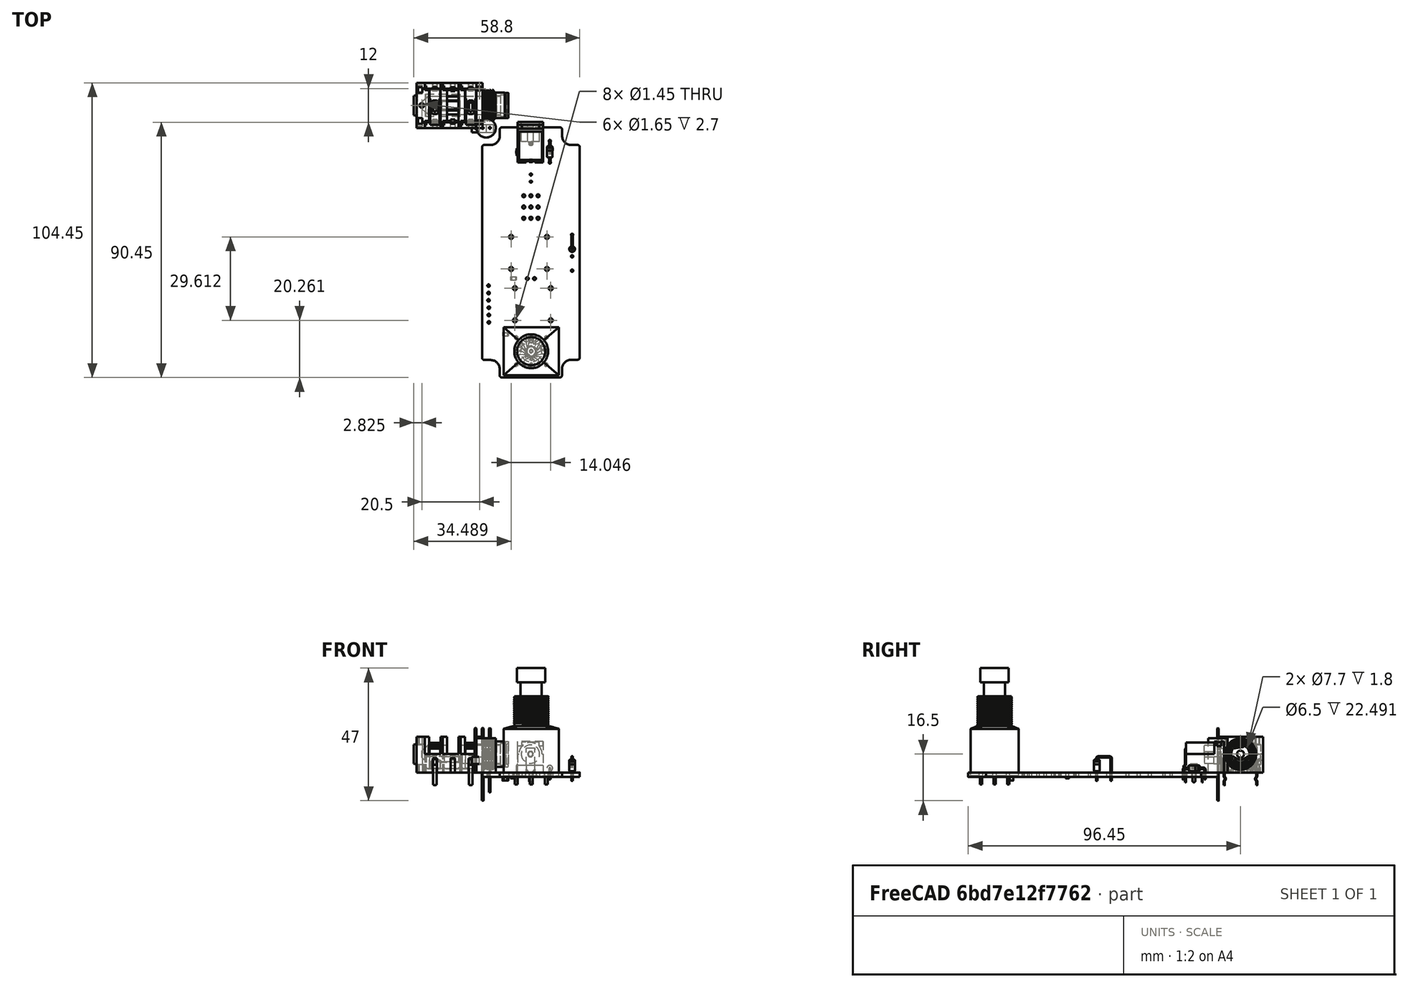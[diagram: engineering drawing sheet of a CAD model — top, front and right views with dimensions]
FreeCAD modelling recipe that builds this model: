
FCSTD DOCUMENT  (FreeCAD 0.20R25645 (Git))
Label: freecad_pcb
License: All rights reserved
LicenseURL: http://en.wikipedia.org/wiki/All_rights_reserved
objects: App::Link×31, Part::Feature×22, App::Part×8, PartDesign::CoordinateSystem×1, Sketcher::SketchObject×1
note: 24 computed .brp shape members not serialized (recipe doc carries the construction recipe); baked Part::Feature solids carry a one-line shape summary decoded from their .brp

FEATURE [PartDesign::CoordinateSystem] Local_CS_ba79
  AttacherType = Attacher::AttachEngine3D
FEATURE [Part::Feature] Pcb_ba79
  Placement = pos=(-82.9,55.9,0) rot=(0,0,1;0rad)
  shape: bbox 34.6 x 88.7 x 1.6 mm, 142 faces (baked)
FEATURE [Sketcher::SketchObject] PCB_Sketch_ba79
  FullyConstrained = false
  sketch-geometry (464):
    g0: LineSegment StartX=33.6003 StartY=-6 StartZ=0 EndX=31.35 EndY=-6 EndZ=0
    g1: LineSegment StartX=34.4 StartY=-81.3503 StartZ=0 EndX=34.4 EndY=-6.79966 EndZ=0
    g2: LineSegment StartX=31.35 StartY=-82.15 StartZ=0 EndX=33.6003 EndY=-82.15 EndZ=0
    g3: LineSegment StartX=28.1 StartY=-87.6503 StartZ=0 EndX=28.1 EndY=-85.4 EndZ=0
    g4: LineSegment StartX=6.79966 StartY=-88.45 StartZ=0 EndX=27.3003 EndY=-88.45 EndZ=0
    g5: LineSegment StartX=-0.2 StartY=-6.79966 StartZ=0 EndX=-0.2 EndY=-81.4503 EndZ=0
    g6: LineSegment StartX=0.599657 StartY=-82.25 StartZ=0 EndX=2.85 EndY=-82.25 EndZ=0
    g7: LineSegment StartX=6 StartY=-85.4 StartZ=0 EndX=6 EndY=-87.6503 EndZ=0
    g8: LineSegment StartX=28.15 StartY=-2.8 StartZ=0 EndX=28.15 EndY=-0.549657 EndZ=0
    g9: LineSegment StartX=27.3503 StartY=0.25 StartZ=0 EndX=6.84966 EndY=0.25 EndZ=0
    g10: LineSegment StartX=6.05 StartY=-0.549657 StartZ=0 EndX=6.05 EndY=-2.8 EndZ=0
    g11: LineSegment StartX=2.85 StartY=-6 StartZ=0 EndX=0.599657 EndY=-6 EndZ=0
    g12: BSplineCurve PolesCount=4 KnotsCount=2 Degree=3 IsPeriodic=0
    g13: BSplineCurve PolesCount=4 KnotsCount=2 Degree=3 IsPeriodic=0
    g14: BSplineCurve PolesCount=4 KnotsCount=2 Degree=3 IsPeriodic=0
    g15: BSplineCurve PolesCount=4 KnotsCount=2 Degree=3 IsPeriodic=0
    g16: BSplineCurve PolesCount=4 KnotsCount=2 Degree=3 IsPeriodic=0
    g17: BSplineCurve PolesCount=4 KnotsCount=2 Degree=3 IsPeriodic=0
    g18: BSplineCurve PolesCount=4 KnotsCount=2 Degree=3 IsPeriodic=0
    g19: BSplineCurve PolesCount=4 KnotsCount=2 Degree=3 IsPeriodic=0
    g20: BSplineCurve PolesCount=4 KnotsCount=2 Degree=3 IsPeriodic=0
    g21: BSplineCurve PolesCount=4 KnotsCount=2 Degree=3 IsPeriodic=0
    g22: BSplineCurve PolesCount=4 KnotsCount=2 Degree=3 IsPeriodic=0
    g23: BSplineCurve PolesCount=4 KnotsCount=2 Degree=3 IsPeriodic=0
    g24: BSplineCurve PolesCount=4 KnotsCount=2 Degree=3 IsPeriodic=0
    g25: BSplineCurve PolesCount=4 KnotsCount=2 Degree=3 IsPeriodic=0
    g26: BSplineCurve PolesCount=4 KnotsCount=2 Degree=3 IsPeriodic=0
    g27: BSplineCurve PolesCount=4 KnotsCount=2 Degree=3 IsPeriodic=0
    g28: BSplineCurve PolesCount=4 KnotsCount=2 Degree=3 IsPeriodic=0
    g29: BSplineCurve PolesCount=4 KnotsCount=2 Degree=3 IsPeriodic=0
    g30: BSplineCurve PolesCount=4 KnotsCount=2 Degree=3 IsPeriodic=0
    g31: BSplineCurve PolesCount=4 KnotsCount=2 Degree=3 IsPeriodic=0
    g32: BSplineCurve PolesCount=4 KnotsCount=2 Degree=3 IsPeriodic=0
    g33: BSplineCurve PolesCount=4 KnotsCount=2 Degree=3 IsPeriodic=0
    g34: BSplineCurve PolesCount=4 KnotsCount=2 Degree=3 IsPeriodic=0
    g35: BSplineCurve PolesCount=4 KnotsCount=2 Degree=3 IsPeriodic=0
    g36: BSplineCurve PolesCount=4 KnotsCount=2 Degree=3 IsPeriodic=0
    g37: BSplineCurve PolesCount=4 KnotsCount=2 Degree=3 IsPeriodic=0
    g38: BSplineCurve PolesCount=4 KnotsCount=2 Degree=3 IsPeriodic=0
    g39: BSplineCurve PolesCount=4 KnotsCount=2 Degree=3 IsPeriodic=0
    g40: BSplineCurve PolesCount=4 KnotsCount=2 Degree=3 IsPeriodic=0
    g41: BSplineCurve PolesCount=4 KnotsCount=2 Degree=3 IsPeriodic=0
    g42: BSplineCurve PolesCount=4 KnotsCount=2 Degree=3 IsPeriodic=0
    g43: BSplineCurve PolesCount=4 KnotsCount=2 Degree=3 IsPeriodic=0
    g44: BSplineCurve PolesCount=4 KnotsCount=2 Degree=3 IsPeriodic=0
    g45: BSplineCurve PolesCount=4 KnotsCount=2 Degree=3 IsPeriodic=0
    g46: BSplineCurve PolesCount=4 KnotsCount=2 Degree=3 IsPeriodic=0
    g47: BSplineCurve PolesCount=4 KnotsCount=2 Degree=3 IsPeriodic=0
    g48: BSplineCurve PolesCount=4 KnotsCount=2 Degree=3 IsPeriodic=0
    g49: BSplineCurve PolesCount=4 KnotsCount=2 Degree=3 IsPeriodic=0
    g50: BSplineCurve PolesCount=4 KnotsCount=2 Degree=3 IsPeriodic=0
    g51: BSplineCurve PolesCount=4 KnotsCount=2 Degree=3 IsPeriodic=0
    g52: BSplineCurve PolesCount=4 KnotsCount=2 Degree=3 IsPeriodic=0
    g53: BSplineCurve PolesCount=4 KnotsCount=2 Degree=3 IsPeriodic=0
    g54: BSplineCurve PolesCount=4 KnotsCount=2 Degree=3 IsPeriodic=0
    g55: BSplineCurve PolesCount=4 KnotsCount=2 Degree=3 IsPeriodic=0
    g56: BSplineCurve PolesCount=4 KnotsCount=2 Degree=3 IsPeriodic=0
    g57: BSplineCurve PolesCount=4 KnotsCount=2 Degree=3 IsPeriodic=0
    g58: BSplineCurve PolesCount=4 KnotsCount=2 Degree=3 IsPeriodic=0
    g59: BSplineCurve PolesCount=4 KnotsCount=2 Degree=3 IsPeriodic=0
    g60: BSplineCurve PolesCount=4 KnotsCount=2 Degree=3 IsPeriodic=0
    g61: BSplineCurve PolesCount=4 KnotsCount=2 Degree=3 IsPeriodic=0
    g62: BSplineCurve PolesCount=4 KnotsCount=2 Degree=3 IsPeriodic=0
    g63: BSplineCurve PolesCount=4 KnotsCount=2 Degree=3 IsPeriodic=0
    g64: BSplineCurve PolesCount=4 KnotsCount=2 Degree=3 IsPeriodic=0
    g65: BSplineCurve PolesCount=4 KnotsCount=2 Degree=3 IsPeriodic=0
    g66: BSplineCurve PolesCount=4 KnotsCount=2 Degree=3 IsPeriodic=0
    g67: BSplineCurve PolesCount=4 KnotsCount=2 Degree=3 IsPeriodic=0
    g68: BSplineCurve PolesCount=4 KnotsCount=2 Degree=3 IsPeriodic=0
    g69: BSplineCurve PolesCount=4 KnotsCount=2 Degree=3 IsPeriodic=0
    g70: BSplineCurve PolesCount=4 KnotsCount=2 Degree=3 IsPeriodic=0
    g71: BSplineCurve PolesCount=4 KnotsCount=2 Degree=3 IsPeriodic=0
    g72: BSplineCurve PolesCount=4 KnotsCount=2 Degree=3 IsPeriodic=0
    g73: BSplineCurve PolesCount=4 KnotsCount=2 Degree=3 IsPeriodic=0
    g74: BSplineCurve PolesCount=4 KnotsCount=2 Degree=3 IsPeriodic=0
    g75: BSplineCurve PolesCount=4 KnotsCount=2 Degree=3 IsPeriodic=0
    g76: ArcOfCircle CenterX=31.35 CenterY=-2.8 CenterZ=0 NormalX=0 NormalY=0 NormalZ=1 AngleXU=0 Radius=3.2 StartAngle=3.14159 EndAngle=4.71239
    g77: ArcOfCircle CenterX=31.35 CenterY=-85.4 CenterZ=0 NormalX=0 NormalY=0 NormalZ=1 AngleXU=0 Radius=3.25 StartAngle=1.5708 EndAngle=3.14159
    g78: ArcOfCircle CenterX=2.85 CenterY=-85.4 CenterZ=0 NormalX=0 NormalY=0 NormalZ=1 AngleXU=0 Radius=3.15 StartAngle=0 EndAngle=1.5708
    g79: ArcOfCircle CenterX=2.85 CenterY=-2.8 CenterZ=0 NormalX=0 NormalY=0 NormalZ=1 AngleXU=0 Radius=3.2 StartAngle=4.71239 EndAngle=6.28319
    g80-g83: Circle x4 (B-spline internal-alignment scaffolding for g12; pole/knot coordinates omitted)
    g84: GeomPoint X=34.3847 Y=-6.64376 Z=0
    g85: GeomPoint X=34.4 Y=-6.79966 Z=0
    g86-g89: Circle x4 (B-spline internal-alignment scaffolding for g13; pole/knot coordinates omitted)
    g90: GeomPoint X=34.3392 Y=-6.49375 Z=0
    g91: GeomPoint X=34.3847 Y=-6.64376 Z=0
    g92-g95: Circle x4 (B-spline internal-alignment scaffolding for g14; pole/knot coordinates omitted)
    g96: GeomPoint X=34.2653 Y=-6.35536 Z=0
    g97: GeomPoint X=34.3392 Y=-6.49375 Z=0
    g98-g101: Circle x4 (B-spline internal-alignment scaffolding for g15; pole/knot coordinates omitted)
    g102: GeomPoint X=34.1658 Y=-6.23417 Z=0
    g103: GeomPoint X=34.2653 Y=-6.35536 Z=0
    g104-g107: Circle x4 (B-spline internal-alignment scaffolding for g16; pole/knot coordinates omitted)
    g108: GeomPoint X=34.0446 Y=-6.13472 Z=0
    g109: GeomPoint X=34.1658 Y=-6.23417 Z=0
    g110-g113: Circle x4 (B-spline internal-alignment scaffolding for g17; pole/knot coordinates omitted)
    g114: GeomPoint X=33.9063 Y=-6.06079 Z=0
    g115: GeomPoint X=34.0446 Y=-6.13472 Z=0
    g116-g119: Circle x4 (B-spline internal-alignment scaffolding for g18; pole/knot coordinates omitted)
    g120: GeomPoint X=33.7562 Y=-6.01533 Z=0
    g121: GeomPoint X=33.9063 Y=-6.06079 Z=0
    g122-g125: Circle x4 (B-spline internal-alignment scaffolding for g19; pole/knot coordinates omitted)
    g126: GeomPoint X=33.6003 Y=-6 Z=0
    g127: GeomPoint X=33.7562 Y=-6.01533 Z=0
    g128-g131: Circle x4 (B-spline internal-alignment scaffolding for g20; pole/knot coordinates omitted)
    g132: GeomPoint X=33.7562 Y=-82.1347 Z=0
    g133: GeomPoint X=33.6003 Y=-82.15 Z=0
    g134-g137: Circle x4 (B-spline internal-alignment scaffolding for g21; pole/knot coordinates omitted)
    g138: GeomPoint X=33.9063 Y=-82.0892 Z=0
    g139: GeomPoint X=33.7562 Y=-82.1347 Z=0
    g140-g143: Circle x4 (B-spline internal-alignment scaffolding for g22; pole/knot coordinates omitted)
    g144: GeomPoint X=34.0446 Y=-82.0153 Z=0
    g145: GeomPoint X=33.9063 Y=-82.0892 Z=0
    g146-g149: Circle x4 (B-spline internal-alignment scaffolding for g23; pole/knot coordinates omitted)
    g150: GeomPoint X=34.1658 Y=-81.9158 Z=0
    g151: GeomPoint X=34.0446 Y=-82.0153 Z=0
    g152-g155: Circle x4 (B-spline internal-alignment scaffolding for g24; pole/knot coordinates omitted)
    g156: GeomPoint X=34.2653 Y=-81.7946 Z=0
    g157: GeomPoint X=34.1658 Y=-81.9158 Z=0
    g158-g161: Circle x4 (B-spline internal-alignment scaffolding for g25; pole/knot coordinates omitted)
    g162: GeomPoint X=34.3392 Y=-81.6563 Z=0
    g163: GeomPoint X=34.2653 Y=-81.7946 Z=0
    g164-g167: Circle x4 (B-spline internal-alignment scaffolding for g26; pole/knot coordinates omitted)
    g168: GeomPoint X=34.3847 Y=-81.5062 Z=0
    g169: GeomPoint X=34.3392 Y=-81.6563 Z=0
    g170-g173: Circle x4 (B-spline internal-alignment scaffolding for g27; pole/knot coordinates omitted)
    g174: GeomPoint X=34.4 Y=-81.3503 Z=0
    g175: GeomPoint X=34.3847 Y=-81.5062 Z=0
    g176-g179: Circle x4 (B-spline internal-alignment scaffolding for g28; pole/knot coordinates omitted)
    g180: GeomPoint X=27.4562 Y=-88.4347 Z=0
    g181: GeomPoint X=27.3003 Y=-88.45 Z=0
    g182-g185: Circle x4 (B-spline internal-alignment scaffolding for g29; pole/knot coordinates omitted)
    g186: GeomPoint X=27.6063 Y=-88.3892 Z=0
    g187: GeomPoint X=27.4562 Y=-88.4347 Z=0
    g188-g191: Circle x4 (B-spline internal-alignment scaffolding for g30; pole/knot coordinates omitted)
    g192: GeomPoint X=27.7446 Y=-88.3153 Z=0
    g193: GeomPoint X=27.6063 Y=-88.3892 Z=0
    g194-g197: Circle x4 (B-spline internal-alignment scaffolding for g31; pole/knot coordinates omitted)
    g198: GeomPoint X=27.8658 Y=-88.2158 Z=0
    g199: GeomPoint X=27.7446 Y=-88.3153 Z=0
    g200-g203: Circle x4 (B-spline internal-alignment scaffolding for g32; pole/knot coordinates omitted)
    g204: GeomPoint X=27.9653 Y=-88.0946 Z=0
    g205: GeomPoint X=27.8658 Y=-88.2158 Z=0
    g206-g209: Circle x4 (B-spline internal-alignment scaffolding for g33; pole/knot coordinates omitted)
    g210: GeomPoint X=28.0392 Y=-87.9563 Z=0
    g211: GeomPoint X=27.9653 Y=-88.0946 Z=0
    g212-g215: Circle x4 (B-spline internal-alignment scaffolding for g34; pole/knot coordinates omitted)
    g216: GeomPoint X=28.0847 Y=-87.8062 Z=0
    g217: GeomPoint X=28.0392 Y=-87.9563 Z=0
    g218-g221: Circle x4 (B-spline internal-alignment scaffolding for g35; pole/knot coordinates omitted)
    g222: GeomPoint X=28.1 Y=-87.6503 Z=0
    g223: GeomPoint X=28.0847 Y=-87.8062 Z=0
    g224-g227: Circle x4 (B-spline internal-alignment scaffolding for g36; pole/knot coordinates omitted)
    g228: GeomPoint X=-0.184668 Y=-81.6062 Z=0
    g229: GeomPoint X=-0.2 Y=-81.4503 Z=0
    g230-g233: Circle x4 (B-spline internal-alignment scaffolding for g37; pole/knot coordinates omitted)
    g234: GeomPoint X=-0.139209 Y=-81.7563 Z=0
    g235: GeomPoint X=-0.184668 Y=-81.6062 Z=0
    g236-g239: Circle x4 (B-spline internal-alignment scaffolding for g38; pole/knot coordinates omitted)
    g240: GeomPoint X=-0.065278 Y=-81.8946 Z=0
    g241: GeomPoint X=-0.139209 Y=-81.7563 Z=0
    g242-g245: Circle x4 (B-spline internal-alignment scaffolding for g39; pole/knot coordinates omitted)
    g246: GeomPoint X=0.034172 Y=-82.0158 Z=0
    g247: GeomPoint X=-0.065278 Y=-81.8946 Z=0
    g248-g251: Circle x4 (B-spline internal-alignment scaffolding for g40; pole/knot coordinates omitted)
    g252: GeomPoint X=0.155365 Y=-82.1153 Z=0
    g253: GeomPoint X=0.034172 Y=-82.0158 Z=0
    g254-g257: Circle x4 (B-spline internal-alignment scaffolding for g41; pole/knot coordinates omitted)
    g258: GeomPoint X=0.293747 Y=-82.1892 Z=0
    g259: GeomPoint X=0.155365 Y=-82.1153 Z=0
    g260-g263: Circle x4 (B-spline internal-alignment scaffolding for g42; pole/knot coordinates omitted)
    g264: GeomPoint X=0.443764 Y=-82.2347 Z=0
    g265: GeomPoint X=0.293747 Y=-82.1892 Z=0
    g266-g269: Circle x4 (B-spline internal-alignment scaffolding for g43; pole/knot coordinates omitted)
    g270: GeomPoint X=0.599657 Y=-82.25 Z=0
    g271: GeomPoint X=0.443764 Y=-82.2347 Z=0
    g272-g275: Circle x4 (B-spline internal-alignment scaffolding for g44; pole/knot coordinates omitted)
    g276: GeomPoint X=6.01533 Y=-87.8062 Z=0
    g277: GeomPoint X=6 Y=-87.6503 Z=0
    g278-g281: Circle x4 (B-spline internal-alignment scaffolding for g45; pole/knot coordinates omitted)
    g282: GeomPoint X=6.06079 Y=-87.9563 Z=0
    g283: GeomPoint X=6.01533 Y=-87.8062 Z=0
    g284-g287: Circle x4 (B-spline internal-alignment scaffolding for g46; pole/knot coordinates omitted)
    g288: GeomPoint X=6.13472 Y=-88.0946 Z=0
    g289: GeomPoint X=6.06079 Y=-87.9563 Z=0
    g290-g293: Circle x4 (B-spline internal-alignment scaffolding for g47; pole/knot coordinates omitted)
    g294: GeomPoint X=6.23417 Y=-88.2158 Z=0
    g295: GeomPoint X=6.13472 Y=-88.0946 Z=0
    g296-g299: Circle x4 (B-spline internal-alignment scaffolding for g48; pole/knot coordinates omitted)
    g300: GeomPoint X=6.35536 Y=-88.3153 Z=0
    g301: GeomPoint X=6.23417 Y=-88.2158 Z=0
    g302-g305: Circle x4 (B-spline internal-alignment scaffolding for g49; pole/knot coordinates omitted)
    g306: GeomPoint X=6.49375 Y=-88.3892 Z=0
    g307: GeomPoint X=6.35536 Y=-88.3153 Z=0
    g308-g311: Circle x4 (B-spline internal-alignment scaffolding for g50; pole/knot coordinates omitted)
    g312: GeomPoint X=6.64376 Y=-88.4347 Z=0
    g313: GeomPoint X=6.49375 Y=-88.3892 Z=0
    g314-g317: Circle x4 (B-spline internal-alignment scaffolding for g51; pole/knot coordinates omitted)
    g318: GeomPoint X=6.79966 Y=-88.45 Z=0
    g319: GeomPoint X=6.64376 Y=-88.4347 Z=0
    g320-g323: Circle x4 (B-spline internal-alignment scaffolding for g52; pole/knot coordinates omitted)
    g324: GeomPoint X=28.1347 Y=-0.393764 Z=0
    g325: GeomPoint X=28.15 Y=-0.549657 Z=0
    g326-g329: Circle x4 (B-spline internal-alignment scaffolding for g53; pole/knot coordinates omitted)
    g330: GeomPoint X=28.0892 Y=-0.243747 Z=0
    g331: GeomPoint X=28.1347 Y=-0.393764 Z=0
    g332-g335: Circle x4 (B-spline internal-alignment scaffolding for g54; pole/knot coordinates omitted)
    g336: GeomPoint X=28.0153 Y=-0.105365 Z=0
    g337: GeomPoint X=28.0892 Y=-0.243747 Z=0
    g338-g341: Circle x4 (B-spline internal-alignment scaffolding for g55; pole/knot coordinates omitted)
    g342: GeomPoint X=27.9158 Y=0.015828 Z=0
    g343: GeomPoint X=28.0153 Y=-0.105365 Z=0
    g344-g347: Circle x4 (B-spline internal-alignment scaffolding for g56; pole/knot coordinates omitted)
    g348: GeomPoint X=27.7946 Y=0.115278 Z=0
    g349: GeomPoint X=27.9158 Y=0.015828 Z=0
    g350-g353: Circle x4 (B-spline internal-alignment scaffolding for g57; pole/knot coordinates omitted)
    g354: GeomPoint X=27.6563 Y=0.189209 Z=0
    g355: GeomPoint X=27.7946 Y=0.115278 Z=0
    g356-g359: Circle x4 (B-spline internal-alignment scaffolding for g58; pole/knot coordinates omitted)
    g360: GeomPoint X=27.5062 Y=0.234668 Z=0
    g361: GeomPoint X=27.6563 Y=0.189209 Z=0
    g362-g365: Circle x4 (B-spline internal-alignment scaffolding for g59; pole/knot coordinates omitted)
    g366: GeomPoint X=27.3503 Y=0.25 Z=0
    g367: GeomPoint X=27.5062 Y=0.234668 Z=0
    g368-g371: Circle x4 (B-spline internal-alignment scaffolding for g60; pole/knot coordinates omitted)
    g372: GeomPoint X=6.69376 Y=0.234668 Z=0
    g373: GeomPoint X=6.84966 Y=0.25 Z=0
    g374-g377: Circle x4 (B-spline internal-alignment scaffolding for g61; pole/knot coordinates omitted)
    g378: GeomPoint X=6.54375 Y=0.189209 Z=0
    g379: GeomPoint X=6.69376 Y=0.234668 Z=0
    g380-g383: Circle x4 (B-spline internal-alignment scaffolding for g62; pole/knot coordinates omitted)
    g384: GeomPoint X=6.40536 Y=0.115278 Z=0
    g385: GeomPoint X=6.54375 Y=0.189209 Z=0
    g386-g389: Circle x4 (B-spline internal-alignment scaffolding for g63; pole/knot coordinates omitted)
    g390: GeomPoint X=6.28417 Y=0.015828 Z=0
    g391: GeomPoint X=6.40536 Y=0.115278 Z=0
    g392-g395: Circle x4 (B-spline internal-alignment scaffolding for g64; pole/knot coordinates omitted)
    g396: GeomPoint X=6.18472 Y=-0.105365 Z=0
    g397: GeomPoint X=6.28417 Y=0.015828 Z=0
    g398-g401: Circle x4 (B-spline internal-alignment scaffolding for g65; pole/knot coordinates omitted)
    g402: GeomPoint X=6.11079 Y=-0.243747 Z=0
    g403: GeomPoint X=6.18472 Y=-0.105365 Z=0
    g404-g407: Circle x4 (B-spline internal-alignment scaffolding for g66; pole/knot coordinates omitted)
    g408: GeomPoint X=6.06533 Y=-0.393764 Z=0
    g409: GeomPoint X=6.11079 Y=-0.243747 Z=0
    g410-g413: Circle x4 (B-spline internal-alignment scaffolding for g67; pole/knot coordinates omitted)
    g414: GeomPoint X=6.05 Y=-0.549657 Z=0
    g415: GeomPoint X=6.06533 Y=-0.393764 Z=0
    g416-g419: Circle x4 (B-spline internal-alignment scaffolding for g68; pole/knot coordinates omitted)
    g420: GeomPoint X=0.443764 Y=-6.01533 Z=0
    g421: GeomPoint X=0.599657 Y=-6 Z=0
    g422-g425: Circle x4 (B-spline internal-alignment scaffolding for g69; pole/knot coordinates omitted)
    g426: GeomPoint X=0.293747 Y=-6.06079 Z=0
    g427: GeomPoint X=0.443764 Y=-6.01533 Z=0
    g428-g431: Circle x4 (B-spline internal-alignment scaffolding for g70; pole/knot coordinates omitted)
    g432: GeomPoint X=0.155365 Y=-6.13472 Z=0
    g433: GeomPoint X=0.293747 Y=-6.06079 Z=0
    g434-g437: Circle x4 (B-spline internal-alignment scaffolding for g71; pole/knot coordinates omitted)
    g438: GeomPoint X=0.034172 Y=-6.23417 Z=0
    g439: GeomPoint X=0.155365 Y=-6.13472 Z=0
    g440-g443: Circle x4 (B-spline internal-alignment scaffolding for g72; pole/knot coordinates omitted)
    g444: GeomPoint X=-0.065278 Y=-6.35536 Z=0
    g445: GeomPoint X=0.034172 Y=-6.23417 Z=0
    g446-g449: Circle x4 (B-spline internal-alignment scaffolding for g73; pole/knot coordinates omitted)
    g450: GeomPoint X=-0.139209 Y=-6.49375 Z=0
    g451: GeomPoint X=-0.065278 Y=-6.35536 Z=0
    g452-g455: Circle x4 (B-spline internal-alignment scaffolding for g74; pole/knot coordinates omitted)
    g456: GeomPoint X=-0.184668 Y=-6.64376 Z=0
    g457: GeomPoint X=-0.139209 Y=-6.49375 Z=0
    g458-g461: Circle x4 (B-spline internal-alignment scaffolding for g75; pole/knot coordinates omitted)
    g462: GeomPoint X=-0.2 Y=-6.79966 Z=0
    g463: GeomPoint X=-0.184668 Y=-6.64376 Z=0
  constraints (144):
    c: Coincident(g36,g5)
    c: Coincident(g75,g5)
    c: Coincident(g36,g37)
    c: Coincident(g75,g74)
    c: Coincident(g37,g38)
    c: Coincident(g74,g73)
    c: Coincident(g39,g38)
    c: Coincident(g72,g73)
    c: Coincident(g39,g40)
    c: Coincident(g72,g71)
    c: Coincident(g41,g40)
    c: Coincident(g71,g70)
    c: Coincident(g42,g41)
    c: Coincident(g69,g70)
    c: Coincident(g43,g42)
    c: Coincident(g68,g69)
    c: Coincident(g6,g43)
    c: Coincident(g11,g68)
    c: Coincident(g6,g78)
    c: Coincident(g11,g79)
    c: Coincident(g44,g7)
    c: Coincident(g7,g78)
    c: Coincident(g44,g45)
    c: Coincident(g79,g10)
    c: Coincident(g10,g67)
    c: Coincident(g46,g45)
    c: Coincident(g67,g66)
    c: Coincident(g65,g66)
    c: Coincident(g47,g46)
    c: Coincident(g64,g65)
    c: Coincident(g48,g47)
    c: Coincident(g64,g63)
    c: Coincident(g48,g49)
    c: Coincident(g63,g62)
    c: Coincident(g50,g49)
    c: Coincident(g62,g61)
    c: Coincident(g51,g50)
    c: Coincident(g60,g61)
    c: Coincident(g4,g51)
    c: Coincident(g60,g9)
    c: Coincident(g4,g28)
    c: Coincident(g9,g59)
    c: Coincident(g29,g28)
    c: Coincident(g58,g59)
    c: Coincident(g29,g30)
    c: Coincident(g58,g57)
    c: Coincident(g31,g30)
    c: Coincident(g57,g56)
    c: Coincident(g32,g31)
    c: Coincident(g56,g55)
    c: Coincident(g32,g33)
    c: Coincident(g54,g55)
    c: Coincident(g34,g33)
    c: Coincident(g35,g34)
    c: Coincident(g53,g54)
    c: Coincident(g3,g35)
    c: Coincident(g77,g3)
    c: Coincident(g53,g52)
    c: Coincident(g76,g8)
    c: Coincident(g52,g8)
    c: Coincident(g77,g2)
    c: Coincident(g0,g76)
    c: Coincident(g2,g20)
    c: Coincident(g0,g19)
    c: Coincident(g21,g20)
    c: Coincident(g19,g18)
    c: Coincident(g22,g21)
    c: Coincident(g17,g18)
    c: Coincident(g23,g22)
    c: Coincident(g17,g16)
    c: Coincident(g23,g24)
    c: Coincident(g16,g15)
    c: Coincident(g24,g25)
    c: Coincident(g14,g15)
    c: Coincident(g25,g26)
    c: Coincident(g13,g14)
    c: Coincident(g27,g26)
    c: Coincident(g13,g12)
    c: Coincident(g27,g1)
    c: Coincident(g12,g1)
    c: InternalAlignment(g80-g85 -> g12) x6
    c: InternalAlignment(g86-g91 -> g13) x6
    c: InternalAlignment(g92-g97 -> g14) x6
    c: InternalAlignment(g98-g103 -> g15) x6
    c: InternalAlignment(g104-g109 -> g16) x6
    c: InternalAlignment(g110-g115 -> g17) x6
    c: InternalAlignment(g116-g121 -> g18) x6
    c: InternalAlignment(g122-g127 -> g19) x6
    c: InternalAlignment(g128-g133 -> g20) x6
    c: InternalAlignment(g134-g139 -> g21) x6
    c: InternalAlignment(g140-g145 -> g22) x6
    c: InternalAlignment(g146-g151 -> g23) x6
    c: InternalAlignment(g152-g157 -> g24) x6
    c: InternalAlignment(g158-g163 -> g25) x6
    c: InternalAlignment(g164-g169 -> g26) x6
    c: InternalAlignment(g170-g175 -> g27) x6
    c: InternalAlignment(g176-g181 -> g28) x6
    c: InternalAlignment(g182-g187 -> g29) x6
    c: InternalAlignment(g188-g193 -> g30) x6
    c: InternalAlignment(g194-g199 -> g31) x6
    c: InternalAlignment(g200-g205 -> g32) x6
    c: InternalAlignment(g206-g211 -> g33) x6
    c: InternalAlignment(g212-g217 -> g34) x6
    c: InternalAlignment(g218-g223 -> g35) x6
    c: InternalAlignment(g224-g229 -> g36) x6
    c: InternalAlignment(g230-g235 -> g37) x6
    c: InternalAlignment(g236-g241 -> g38) x6
    c: InternalAlignment(g242-g247 -> g39) x6
    c: InternalAlignment(g248-g253 -> g40) x6
    c: InternalAlignment(g254-g259 -> g41) x6
    c: InternalAlignment(g260-g265 -> g42) x6
    c: InternalAlignment(g266-g271 -> g43) x6
    c: InternalAlignment(g272-g277 -> g44) x6
    c: InternalAlignment(g278-g283 -> g45) x6
    c: InternalAlignment(g284-g289 -> g46) x6
    c: InternalAlignment(g290-g295 -> g47) x6
    c: InternalAlignment(g296-g301 -> g48) x6
    c: InternalAlignment(g302-g307 -> g49) x6
    c: InternalAlignment(g308-g313 -> g50) x6
    c: InternalAlignment(g314-g319 -> g51) x6
    c: InternalAlignment(g320-g325 -> g52) x6
    c: InternalAlignment(g326-g331 -> g53) x6
    c: InternalAlignment(g332-g337 -> g54) x6
    c: InternalAlignment(g338-g343 -> g55) x6
    c: InternalAlignment(g344-g349 -> g56) x6
    c: InternalAlignment(g350-g355 -> g57) x6
    c: InternalAlignment(g356-g361 -> g58) x6
    c: InternalAlignment(g362-g367 -> g59) x6
    c: InternalAlignment(g368-g373 -> g60) x6
    c: InternalAlignment(g374-g379 -> g61) x6
    c: InternalAlignment(g380-g385 -> g62) x6
    c: InternalAlignment(g386-g391 -> g63) x6
    c: InternalAlignment(g392-g397 -> g64) x6
    c: InternalAlignment(g398-g403 -> g65) x6
    c: InternalAlignment(g404-g409 -> g66) x6
    c: InternalAlignment(g410-g415 -> g67) x6
    c: InternalAlignment(g416-g421 -> g68) x6
    c: InternalAlignment(g422-g427 -> g69) x6
    c: InternalAlignment(g428-g433 -> g70) x6
    c: InternalAlignment(g434-g439 -> g71) x6
    c: InternalAlignment(g440-g445 -> g72) x6
    c: InternalAlignment(g446-g451 -> g73) x6
    c: InternalAlignment(g452-g457 -> g74) x6
    c: InternalAlignment(g458-g463 -> g75) x6
FEATURE [App::Part] Board_Geoms_ba79
  Group = -> [Local_CS_ba79,Pcb_ba79,PCB_Sketch_ba79]
  Origin = -> Origin
FEATURE [Part::Feature] Shape  label="D2_D_DO-35_SOD27_P5.08mm_Vertical_KathodeUp_614ABF67"
  Placement = pos=(31.7,-37.82,0) rot=(0,0,-1;1.5708rad)
  shape: bbox 2.165 x 6.474 x 8.812 mm, 17 faces (baked)
FEATURE [Part::Feature] Shape001  label="SW1_FS57003PLT2B2M2QE_614909C1"
  Placement = pos=(17.2,-79.1264,0) rot=(0,0,1;3.14159rad)
  shape: bbox 19.6 x 17 x 41.2 mm, 79 faces (baked)
FEATURE [Part::Feature] Part__Feature  label="Shroud"
  Placement = pos=(2.54,-0.1,3.05) rot=(0,0,1;0rad)
  shape: bbox 2.54 x 2.8 x 2.54 mm, 6 faces (baked)
FEATURE [Part::Feature] Part__Feature001  label="Pin"
  Placement = pos=(2.54,-0.1,3.05) rot=(0,0,1;0rad)
  shape: bbox 0.62 x 0.62 x 15.88 mm, 14 faces (baked)
FEATURE [Part::Feature] Part__Feature002  label="Shroud001"
  Placement = pos=(0,-0.1,3.05) rot=(0,0,1;0rad)
  shape: bbox 2.54 x 2.8 x 2.54 mm, 6 faces (baked)
FEATURE [Part::Feature] Part__Feature003  label="Pin001"
  Placement = pos=(0,-0.1,3.05) rot=(0,0,1;0rad)
  shape: bbox 0.62 x 0.62 x 15.88 mm, 14 faces (baked)
FEATURE [Part::Feature] Part__Feature004  label="Shroud002"
  Placement = pos=(-2.54,-0.1,3.05) rot=(0,0,1;0rad)
  shape: bbox 2.54 x 2.8 x 2.54 mm, 6 faces (baked)
FEATURE [Part::Feature] Part__Feature005  label="Pin002"
  Placement = pos=(-2.54,-0.1,3.05) rot=(0,0,1;0rad)
  shape: bbox 0.62 x 0.62 x 15.88 mm, 14 faces (baked)
FEATURE [App::Part] _5160_195_03LF  label="R21_75160-195-03LF_61490F57"
  Group = -> [Part__Feature,Part__Feature001,Part__Feature002,Part__Feature003,Part__Feature004,Part__Feature005]
  Origin = -> Origin008
  Placement = pos=(17.0746,-28.0216,-3.048) rot=(0,0,1;0rad)
FEATURE [App::Link] R21_75160_195_03LF_61490F57_ln_  label="R20_75160-195-03LF_6148EF5C"
  LinkPlacement = pos=(17.0746,-24.0338,-3.048) rot=(0,0,1;0rad)
  LinkedObject = -> _5160_195_03LF
  Placement = pos=(17.0746,-24.0338,-3.048) rot=(0,0,1;0rad)
FEATURE [App::Link] R21_75160_195_03LF_61490F57_ln_001  label="R19_75160-195-03LF_6148E81B"
  LinkPlacement = pos=(17.0746,-32.0094,-3.048) rot=(0,0,1;0rad)
  LinkedObject = -> _5160_195_03LF
  Placement = pos=(17.0746,-32.0094,-3.048) rot=(0,0,1;0rad)
FEATURE [Part::Feature] Shape002  label="J3_CUI_DEVICES_PJ-102A_6148E860"
  Placement = pos=(16.9499,2.18408,6.50748) rot=(0.57735,0.57735,0.57735;2.0944rad)
  shape: bbox 9.4 x 14.4 x 14.5 mm, 59 faces (baked)
FEATURE [Part::Feature] Part__Feature006  label="PART1"
  Placement = pos=(-11.7,8,6.4) rot=(0,0,1;0rad)
  shape: bbox 32.51 x 16.01 x 12.71 mm, 318 faces (baked)
FEATURE [Part::Feature] Part__Feature007  label="ACJS-HHDR MODEL"
  Placement = pos=(-318.873,-100.46,9e-16) rot=(0,0,1;0rad)
  shape: bbox 3.9 x 1.7 x 13 mm, 26 faces (baked)
FEATURE [Part::Feature] Part__Feature008  label="ACJS-HHDR MODEL001"
  Placement = pos=(-318.873,-100.46,9e-16) rot=(0,0,1;0rad)
  shape: bbox 3.9 x 13.79 x 15 mm, 45 faces (baked)
FEATURE [Part::Feature] Part__Feature009  label="ACJS-HHDR MODEL002"
  Placement = pos=(-318.873,-100.46,9e-16) rot=(0,0,1;0rad)
  shape: bbox 3.9 x 13.79 x 15 mm, 45 faces (baked)
FEATURE [Part::Feature] Part__Feature010  label="ACJS-HHDR MODEL003"
  Placement = pos=(-318.873,-100.46,9e-16) rot=(0,0,1;0rad)
  shape: bbox 3.9 x 1.7 x 13 mm, 26 faces (baked)
FEATURE [Part::Feature] Part__Feature011  label="~PART1"
  Placement = pos=(6.1,8,6.5) rot=(0,0,1;0rad)
  shape: bbox 6 x 9.633 x 9.633 mm, 12 faces (baked)
FEATURE [App::Part] ACJS_HHDR  label="J2_ACJS-HHDR_614900F5"
  Group = -> [Part__Feature006,Part__Feature007,Part__Feature008,Part__Feature009,Part__Feature010,Part__Feature011]
  Origin = -> Origin009
  Placement = pos=(5.8984,-36.302,0) rot=(0,0,1;3.14159rad)
FEATURE [App::Link] J2_ACJS_HHDR_614900F5_ln_  label="J1_ACJS-HHDR_6148EFF9"
  LinkPlacement = pos=(28.3266,-70.465,0) rot=(0,0,1;0rad)
  LinkedObject = -> ACJS_HHDR
  Placement = pos=(28.3266,-70.465,0) rot=(0,0,1;0rad)
FEATURE [Part::Feature] Part__Feature012  label="SimpleBody"
  Placement = pos=(1.25,0,0) rot=(0,0,1;0rad)
  shape: bbox 6.8 x 6.8 x 12.2 mm, 3 faces (baked)
FEATURE [Part::Feature] Part__Feature013  label="Pin1"
  Placement = pos=(0,0,-10) rot=(0,0,1;0rad)
  shape: bbox 0.55 x 0.55 x 10 mm, 3 faces (baked)
FEATURE [Part::Feature] Part__Feature014  label="Pin2"
  Placement = pos=(2.5,0,-7) rot=(0,0,1;0rad)
  shape: bbox 0.55 x 0.55 x 7 mm, 3 faces (baked)
FEATURE [App::Part] ASSEMBLY  label="C12_ASSEMBLY_614A9C1D"
  Group = -> [Part__Feature012,Part__Feature013,Part__Feature014]
  Origin = -> Origin010
  Placement = pos=(17.1,-16.5,0) rot=(0,0,-1;1.5708rad)
FEATURE [Part::Feature] Shape003  label="R23_R_0805_2012Metric_6148E9F2"
  Placement = pos=(10.9,-53.3,-1.6) rot=(1,0,0;3.14159rad)
  shape: bbox 2 x 1.2 x 0.45 mm, 26 faces (baked)
FEATURE [App::Link] R23_R_0805_2012Metric_6148E9F2_ln_  label="R22_R_0805_2012Metric_6148EB45"
  LinkPlacement = pos=(19.9,-77.3,-1.6) rot=(0,1,0;3.14159rad)
  LinkedObject = -> Shape003
  Placement = pos=(19.9,-77.3,-1.6) rot=(0,1,0;3.14159rad)
FEATURE [App::Link] R23_R_0805_2012Metric_6148E9F2_ln_001  label="R18_R_0805_2012Metric_6149DD90"
  LinkPlacement = pos=(31.9,-35.3,0) rot=(0,0,1;3.14159rad)
  LinkedObject = -> Shape003
  Placement = pos=(31.9,-35.3,0) rot=(0,0,1;3.14159rad)
FEATURE [App::Link] R23_R_0805_2012Metric_6148E9F2_ln_002  label="R17_R_0805_2012Metric_6149537A"
  LinkPlacement = pos=(24.3,-33.7,-1.6) rot=(-0.707107,0.707107,0;3.14159rad)
  LinkedObject = -> Shape003
  Placement = pos=(24.3,-33.7,-1.6) rot=(-0.707107,0.707107,0;3.14159rad)
FEATURE [App::Link] R23_R_0805_2012Metric_6148E9F2_ln_003  label="R16_R_0805_2012Metric_6148EA2B"
  LinkPlacement = pos=(12.5,-18.7,0) rot=(0,0,-1;1.5708rad)
  LinkedObject = -> Shape003
  Placement = pos=(12.5,-18.7,0) rot=(0,0,-1;1.5708rad)
FEATURE [App::Link] R23_R_0805_2012Metric_6148E9F2_ln_004  label="R15_R_0805_2012Metric_6148EAEE"
  LinkPlacement = pos=(6.9,-70.1,-1.6) rot=(0.707107,0.707107,0;3.14159rad)
  LinkedObject = -> Shape003
  Placement = pos=(6.9,-70.1,-1.6) rot=(0.707107,0.707107,0;3.14159rad)
FEATURE [App::Link] R23_R_0805_2012Metric_6148E9F2_ln_005  label="R14_R_0805_2012Metric_6148EB75"
  LinkPlacement = pos=(10.3,-70.7,-1.6) rot=(1,0,0;3.14159rad)
  LinkedObject = -> Shape003
  Placement = pos=(10.3,-70.7,-1.6) rot=(1,0,0;3.14159rad)
FEATURE [App::Link] R23_R_0805_2012Metric_6148E9F2_ln_006  label="R13_R_0805_2012Metric_6148EBD8"
  LinkPlacement = pos=(13.5,-71.5,-1.6) rot=(0.707107,0.707107,0;3.14159rad)
  LinkedObject = -> Shape003
  Placement = pos=(13.5,-71.5,-1.6) rot=(0.707107,0.707107,0;3.14159rad)
FEATURE [App::Link] R23_R_0805_2012Metric_6148E9F2_ln_007  label="R12_R_0805_2012Metric_614A5AB1"
  LinkPlacement = pos=(1.3,-72.6,0) rot=(0,0,1;1.5708rad)
  LinkedObject = -> Shape003
  Placement = pos=(1.3,-72.6,0) rot=(0,0,1;1.5708rad)
FEATURE [App::Link] R23_R_0805_2012Metric_6148E9F2_ln_008  label="R11_R_0805_2012Metric_6148ED0D"
  LinkPlacement = pos=(23.7,-15.5,0) rot=(0,0,1;1.5708rad)
  LinkedObject = -> Shape003
  Placement = pos=(23.7,-15.5,0) rot=(0,0,1;1.5708rad)
FEATURE [App::Link] R23_R_0805_2012Metric_6148E9F2_ln_009  label="R10_R_0805_2012Metric_6148ED3D"
  LinkPlacement = pos=(10.5,-14.9,0) rot=(0,0,1;1.5708rad)
  LinkedObject = -> Shape003
  Placement = pos=(10.5,-14.9,0) rot=(0,0,1;1.5708rad)
FEATURE [App::Link] R23_R_0805_2012Metric_6148E9F2_ln_010  label="R9_R_0805_2012Metric_6148EEBD"
  LinkPlacement = pos=(12.5,-14.9,0) rot=(0,0,-1;1.5708rad)
  LinkedObject = -> Shape003
  Placement = pos=(12.5,-14.9,0) rot=(0,0,-1;1.5708rad)
FEATURE [App::Link] R23_R_0805_2012Metric_6148E9F2_ln_011  label="R8_R_0805_2012Metric_6148EC08"
  LinkPlacement = pos=(13.5,-38.9,-1.6) rot=(-0.707107,0.707107,0;3.14159rad)
  LinkedObject = -> Shape003
  Placement = pos=(13.5,-38.9,-1.6) rot=(-0.707107,0.707107,0;3.14159rad)
FEATURE [App::Link] R23_R_0805_2012Metric_6148E9F2_ln_012  label="R7_R_0805_2012Metric_6149A12F"
  LinkPlacement = pos=(23.7,-29.5,-1.6) rot=(1,0,0;3.14159rad)
  LinkedObject = -> Shape003
  Placement = pos=(23.7,-29.5,-1.6) rot=(1,0,0;3.14159rad)
FEATURE [App::Link] R23_R_0805_2012Metric_6148E9F2_ln_013  label="R6_R_0805_2012Metric_6149D317"
  LinkPlacement = pos=(30.8,-22.3,-1.6) rot=(-0.707107,0.707107,0;3.14159rad)
  LinkedObject = -> Shape003
  Placement = pos=(30.8,-22.3,-1.6) rot=(-0.707107,0.707107,0;3.14159rad)
FEATURE [App::Link] R23_R_0805_2012Metric_6148E9F2_ln_014  label="R5_R_0805_2012Metric_6148EDCD"
  LinkPlacement = pos=(16.9,-45.7,-1.6) rot=(0.707107,0.707107,0;3.14159rad)
  LinkedObject = -> Shape003
  Placement = pos=(16.9,-45.7,-1.6) rot=(0.707107,0.707107,0;3.14159rad)
FEATURE [App::Link] R23_R_0805_2012Metric_6148E9F2_ln_015  label="R3_R_0805_2012Metric_614939F4"
  LinkPlacement = pos=(10.7,-43.5,-1.6) rot=(0.707107,0.707107,0;3.14159rad)
  LinkedObject = -> Shape003
  Placement = pos=(10.7,-43.5,-1.6) rot=(0.707107,0.707107,0;3.14159rad)
FEATURE [App::Link] R23_R_0805_2012Metric_6148E9F2_ln_016  label="R2_R_0805_2012Metric_6148E917"
  LinkPlacement = pos=(7.5,-76.9,-1.6) rot=(1,0,0;3.14159rad)
  LinkedObject = -> Shape003
  Placement = pos=(7.5,-76.9,-1.6) rot=(1,0,0;3.14159rad)
FEATURE [App::Link] R23_R_0805_2012Metric_6148E9F2_ln_017  label="R1_R_0805_2012Metric_6148E947"
  LinkPlacement = pos=(11.3,-76.9,-1.6) rot=(1,0,0;3.14159rad)
  LinkedObject = -> Shape003
  Placement = pos=(11.3,-76.9,-1.6) rot=(1,0,0;3.14159rad)
FEATURE [Part::Feature] Shape004  label="D5_D_DO-35_SOD27_P7.62mm_Horizontal_6148EC6D"
  Placement = pos=(23.78,-4.6028,0) rot=(0,0,-1;1.5708rad)
  shape: bbox 2.165 x 8.244 x 5.082 mm, 16 faces, 2 solids (baked)
FEATURE [App::Link] D2_D_DO_35_SOD27_P5_08mm_Vertical_KathodeUp_614ABF67_ln_  label="D1_D_DO-35_SOD27_P5.08mm_Vertical_KathodeUp_6148ECDD"
  LinkPlacement = pos=(31.7,-45.5,0) rot=(0,0,-1;1.5708rad)
  LinkedObject = -> Shape
  Placement = pos=(31.7,-45.5,0) rot=(0,0,-1;1.5708rad)
FEATURE [Part::Feature] Shape005  label="C11_C_0805_2012Metric_6148E70D"
  Placement = pos=(8.0625,-73.1,-1.6) rot=(1,0,0;3.14159rad)
  shape: bbox 2 x 1.25 x 1.25 mm, 28 faces (baked)
FEATURE [App::Link] C11_C_0805_2012Metric_6148E70D_ln_  label="C10_C_0805_2012Metric_61498D01"
  LinkPlacement = pos=(6.3625,-63.7,0) rot=(0,0,1;0rad)
  LinkedObject = -> Shape005
  Placement = pos=(6.3625,-63.7,0) rot=(0,0,1;0rad)
FEATURE [App::Link] C11_C_0805_2012Metric_6148E70D_ln_001  label="C9_C_0805_2012Metric_6148EF26"
  LinkPlacement = pos=(23.7,-19.4625,0) rot=(0,0,-1;1.5708rad)
  LinkedObject = -> Shape005
  Placement = pos=(23.7,-19.4625,0) rot=(0,0,-1;1.5708rad)
FEATURE [App::Link] C11_C_0805_2012Metric_6148E70D_ln_002  label="C8_C_0805_2012Metric_6148E8E4"
  LinkPlacement = pos=(26.5375,-37.3,-1.6) rot=(1,0,0;3.14159rad)
  LinkedObject = -> Shape005
  Placement = pos=(26.5375,-37.3,-1.6) rot=(1,0,0;3.14159rad)
FEATURE [App::Link] C11_C_0805_2012Metric_6148E70D_ln_003  label="C7_C_0805_2012Metric_6149148B"
  LinkPlacement = pos=(9.9,-9.7,0) rot=(0,0,1;1.5708rad)
  LinkedObject = -> Shape005
  Placement = pos=(9.9,-9.7,0) rot=(0,0,1;1.5708rad)
FEATURE [App::Part] Top_ba79
  Group = -> [Shape,Shape001,_5160_195_03LF,R21_75160_195_03LF_61490F57_ln_,R21_75160_195_03LF_61490F57_ln_001,Shape002,ACJS_HHDR,J2_ACJS_HHDR_614900F5_ln_,ASSEMBLY,R23_R_0805_2012Metric_6148E9F2_ln_001,R23_R_0805_2012Metric_6148E9F2_ln_003,R23_R_0805_2012Metric_6148E9F2_ln_007,R23_R_0805_2012Metric_6148E9F2_ln_008,R23_R_0805_2012Metric_6148E9F2_ln_009,R23_R_0805_2012Metric_6148E9F2_ln_010,Shape004,+4 more]
  Origin = -> Origin003
FEATURE [App::Link] C11_C_0805_2012Metric_6148E70D_ln_004  label="C5_C_0805_2012Metric_6148ED9D"
  LinkPlacement = pos=(11.6625,-35.5,-1.6) rot=(0,1,0;3.14159rad)
  LinkedObject = -> Shape005
  Placement = pos=(11.6625,-35.5,-1.6) rot=(0,1,0;3.14159rad)
FEATURE [App::Link] C11_C_0805_2012Metric_6148E70D_ln_005  label="C4_C_0805_2012Metric_6148EBA5"
  LinkPlacement = pos=(19.9,-44.9,-1.6) rot=(1,0,0;3.14159rad)
  LinkedObject = -> Shape005
  Placement = pos=(19.9,-44.9,-1.6) rot=(1,0,0;3.14159rad)
FEATURE [App::Link] C11_C_0805_2012Metric_6148E70D_ln_006  label="C3_C_0805_2012Metric_6149C870"
  LinkPlacement = pos=(29.8,-25.4,-1.6) rot=(1,0,0;3.14159rad)
  LinkedObject = -> Shape005
  Placement = pos=(29.8,-25.4,-1.6) rot=(1,0,0;3.14159rad)
FEATURE [App::Link] C11_C_0805_2012Metric_6148E70D_ln_007  label="C2_C_0805_2012Metric_614A9BA2"
  LinkPlacement = pos=(13.9,-45.7375,-1.6) rot=(0.707107,0.707107,0;3.14159rad)
  LinkedObject = -> Shape005
  Placement = pos=(13.9,-45.7375,-1.6) rot=(0.707107,0.707107,0;3.14159rad)
FEATURE [App::Link] C11_C_0805_2012Metric_6148E70D_ln_008  label="C1_C_0805_2012Metric_6148E73D"
  LinkPlacement = pos=(15.3,-76.9,-1.6) rot=(1,0,0;3.14159rad)
  LinkedObject = -> Shape005
  Placement = pos=(15.3,-76.9,-1.6) rot=(1,0,0;3.14159rad)
FEATURE [App::Part] Bot_ba79
  Group = -> [Shape003,R23_R_0805_2012Metric_6148E9F2_ln_,R23_R_0805_2012Metric_6148E9F2_ln_002,R23_R_0805_2012Metric_6148E9F2_ln_004,R23_R_0805_2012Metric_6148E9F2_ln_005,R23_R_0805_2012Metric_6148E9F2_ln_006,R23_R_0805_2012Metric_6148E9F2_ln_011,R23_R_0805_2012Metric_6148E9F2_ln_012,R23_R_0805_2012Metric_6148E9F2_ln_013,R23_R_0805_2012Metric_6148E9F2_ln_014,R23_R_0805_2012Metric_6148E9F2_ln_015,+9 more]
  Origin = -> Origin004
FEATURE [App::Part] Step_Models_ba79
  Group = -> [Top_ba79,Bot_ba79]
  Origin = -> Origin002
FEATURE [App::Part] Board_ba79  label="MainBoard"
  Group = -> [Board_Geoms_ba79,Step_Models_ba79]
  Origin = -> Origin001
